# Revit family: BE_24686_de_DE
name_source: partatom
category: Leuchten
units: mm (PartAtom-declared; Revit-internal decimal feet)

## family parameters
Basisbauteil = Fläche
Beim Laden mit Abzugskörper schneiden = Ja
Bemaßung runder Anschluss = Durchmesser verwenden
Gemeinsam genutzt = Nein
Lichtquelle = Ja
Raumberechnungspunkt = Ja
Teiletyp = Normal

## types (4) — shared parameters
AC/DC = AC/DC
Aktualisierung = 2022-05-18T04:00:07
BEGA_Dummy = Nein
BEGA_IES = Ja
BEGA_Intern = Ja
BEGA_Intern_Konstruktion = Ja
BEGA_Intern_an = Ja
BEGA_Intern_aus = Ja
Beschreibung = Deckeneinbau-Tiefstrahler
Beschreibung_Sonderanfertigung = Hier können Sie Informationen zur Sonderanfertigung eintragen.
Bestellnummer_Einbaugehäuse = ---
CE_Konformität = ja
ENEC = ja
Einbau_in_Wärmedämmung = ungeeignet
Einbaugehäuse = Nein
Einbautiefe = 70 mm
Einbauöffnung = 177 x 177 mm
Energieeffizienzklasse = LED A++ - A
Farbfilter = 16777215
Farbtemperaturverschiebung bei Dämpfen der Lampe = <Keine Auswahl>
Farbwiedergabeindex = CRI > 80
Frequenz = 0/50-60 Hz
Gewicht = 1.75 kg
Hersteller = BEGA
Lampe = LED 32.8 W
Lastklassifizierung = Beleuchtung
Lebensdauerkriterien = L70B50 @ 25 °C = 180000 h
Logo = BEGA_Logo.png
M_G = Nein
Material_02 = BEGA_Oberfläche_Silber_matt
Material_03 = BEGA_Oberfläche_Weiss_matt
Material_06 = BEGA_Oberfläche_Edelstahl_gebürstet
Material_09 = BEGA_Glas_klar
Material_11 = BEGA_Glas_opal
Material_15 = BEGA_Leuchtmedium_matt
Material_17 = BEGA_Reflektor
Material_20 = BEGA_Platte_Weiss
Neigungswinkel = 0.00°
Netzteil_DALI_steuerbar = Nein
Netzteil_dimmbar_1_bis_10V = Nein
Produktdatenblatt = https://cdn.bega.com
Scheinlast = 0 VA
Schutzart = IP 65
Schutzklasse = II
Sonderanfertigung = Nein
Spannung = 240 V
Strom = 0,7 A
URL = https://www.bega.com
Umgebungstemperatur = 25 °C
zero-valued in all types: Vorgabe-Ansicht

## per-type parameters (varying)
| type | Bestellnummer | Datei für fotometrisches Netz | Farbtemperatur | LED_Modulbezeichnung | Lampenlichtstrom | Leuchtenlichtstrom | M_A | M_W | Modell |
| BEGA_24686_Weiß_K3 | 24686K3 | BE_24686K3.IES | 3000 K | 4x LED-1107/830 | 5540 lm | 3891 lm | Nein | Ja | 24686K3 |
| BEGA_24686_Silber_K4 | 24686AK4 | BE_24686K4.IES | 4000 K | 4x LED-1107/840 | 5600 lm | 3933 lm | Ja | Nein | 24686AK4 |
| BEGA_24686_Silber_K3 | 24686AK3 | BE_24686K3.IES | 3000 K | 4x LED-1107/830 | 5540 lm | 3891 lm | Ja | Nein | 24686AK3 |
| BEGA_24686_Weiß_K4 | 24686K4 | BE_24686K4.IES | 4000 K | 4x LED-1107/840 | 5600 lm | 3933 lm | Nein | Ja | 24686K4 |
